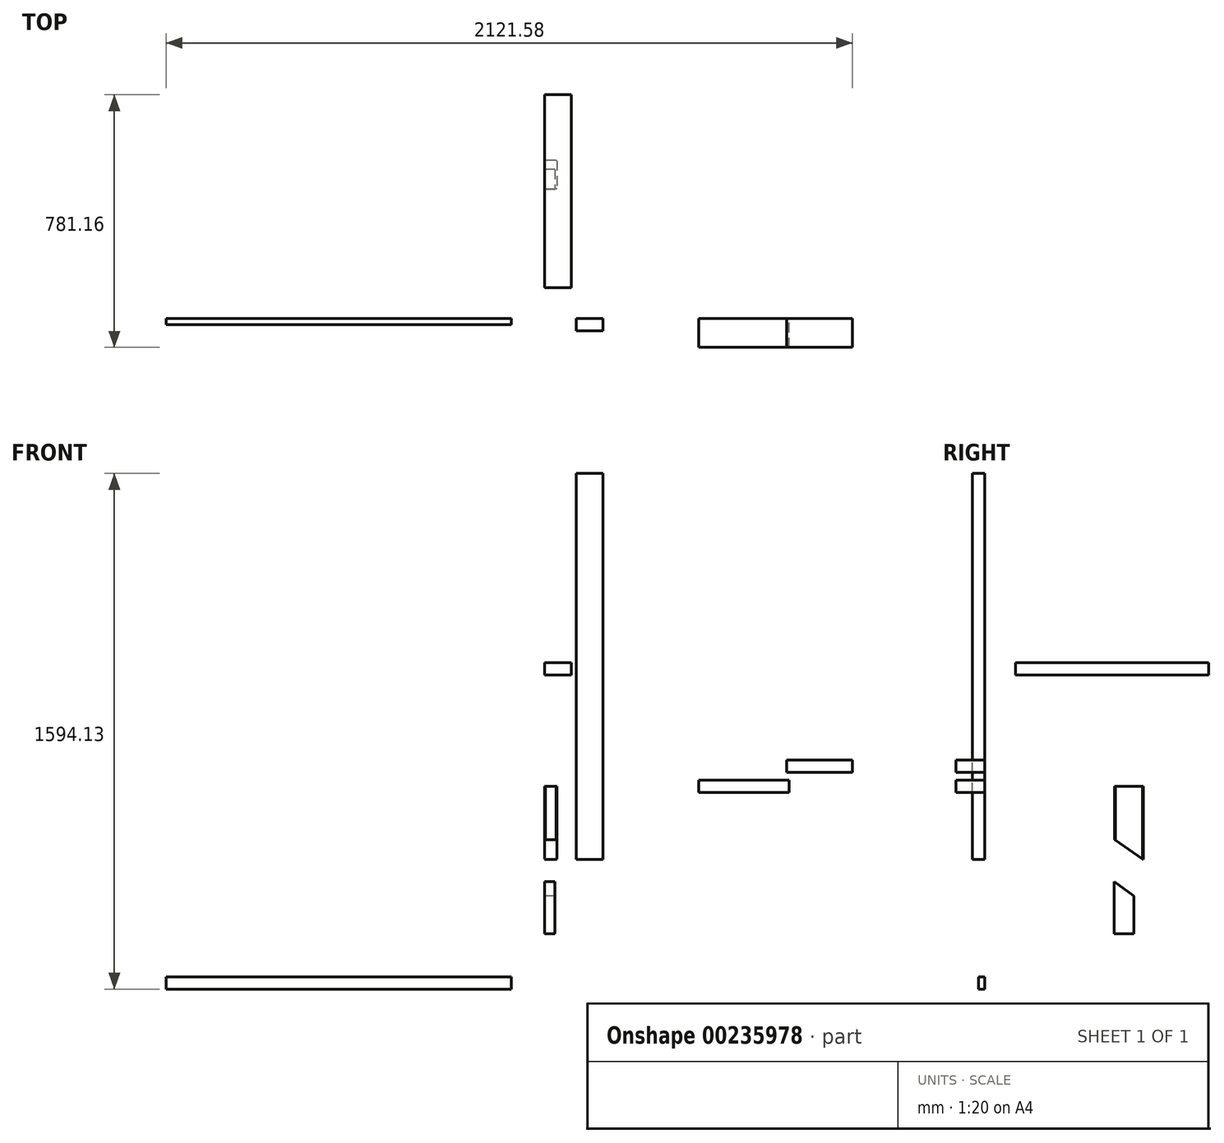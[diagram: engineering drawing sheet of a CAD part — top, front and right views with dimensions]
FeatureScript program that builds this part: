
annotation { "Feature Type Name" : "Feature", "Feature Type Description" : "" }
export const myFeature = defineFeature(function(context is Context, id is Id, definition is map)
    precondition{}
    {
        {
            var Q0;
            Q0=qCreatedBy(makeId("Front.planeOp"),FACE);
            var sketch = newSketch(context, id + "F0", { "sketchPlane" : qUnion([Q0])});
            skLineSegment(sketch, "E0.bottom", {"start": v(0, 0) * mm, "end": v(88.9, 0) * mm});
            skLineSegment(sketch, "E0.top", {"start": v(0, 254) * mm, "end": v(88.9, 254) * mm});
            skLineSegment(sketch, "E0.left", {"start": v(0, 0) * mm, "end": v(0, 254) * mm});
            skLineSegment(sketch, "E0.right", {"start": v(88.9, 0) * mm, "end": v(88.9, 254) * mm});
            skSolve(sketch);
        }
        {
            var Q0;
            Q0 = qSketchRegion(id + "F0", true);
            extrude(context, id + "F1", {"entities" : qUnion([Q0]), "depth" : 38.1 * mm});
        }
        {
            var Q0;
            Q0=makeQuery(id+"F1.opExtrude","CAP_EDGE",EDGE,{"disambiguationData":[OSD([sQuery(id+"F0.wireOp",EDGE,"E0.left")])],"isStart":true});
            var Q1;
            Q1=makeQuery(id+"F1.opExtrude","CAP_EDGE",EDGE,{"disambiguationData":[OSD([sQuery(id+"F0.wireOp",EDGE,"E0.left")])],"isStart":false});
            var Q2;
            Q2=makeQuery(id+"F1.opExtrude","CAP_EDGE",EDGE,{"disambiguationData":[OSD([sQuery(id+"F0.wireOp",EDGE,"E0.right")])],"isStart":false});
            var Q3;
            Q3=makeQuery(id+"F1.opExtrude","CAP_EDGE",EDGE,{"disambiguationData":[OSD([sQuery(id+"F0.wireOp",EDGE,"E0.right")])],"isStart":true});
            fillet(context, id + "F2", {"entities" : qUnion([Q0, Q1, Q2, Q3]), "radius" : 2.54 * mm, "tangentPropagation" : true, "allowEdgeOverflow" : false});
        }
        {
            var Q0;
            Q0=qCreatedBy(makeId("Front.planeOp"),FACE);
            var sketch = newSketch(context, id + "F3", { "sketchPlane" : qUnion([Q0])});
            skLineSegment(sketch, "E1.bottom", {"start": v(98.15, 0) * mm, "end": v(180.7, 0) * mm});
            skLineSegment(sketch, "E1.top", {"start": v(98.15, 1193.8) * mm, "end": v(180.7, 1193.8) * mm});
            skLineSegment(sketch, "E1.left", {"start": v(98.15, 0) * mm, "end": v(98.15, 1193.8) * mm});
            skLineSegment(sketch, "E1.right", {"start": v(180.7, 0) * mm, "end": v(180.7, 1193.8) * mm});
            skSolve(sketch);
        }
        {
            var Q0;
            Q0 = qSketchRegion(id + "F3", true);
            extrude(context, id + "F4", {"entities" : qUnion([Q0]), "depth" : 38.1 * mm});
        }
        {
            var Q0;
            Q0=qCreatedBy(makeId("Right.planeOp"),FACE);
            var sketch = newSketch(context, id + "F5", { "sketchPlane" : qUnion([Q0])});
            skLineSegment(sketch, "E2.top", {"start": v(421.64, 298.64) * mm, "end": v(459.74, 298.64) * mm});
            skLineSegment(sketch, "E2.right", {"start": v(459.74, 44.64) * mm, "end": v(459.74, 298.64) * mm});
            skLineSegment(sketch, "E3", {"start": v(421.64, 298.64) * mm, "end": v(421.64, 82.74) * mm});
            skLineSegment(sketch, "E4", {"start": v(421.64, 82.74) * mm, "end": v(459.74, 44.64) * mm});
            skSolve(sketch);
        }
        {
            var Q0;
            Q0 = qSketchRegion(id + "F5", true);
            extrude(context, id + "F6", {"entities" : qUnion([Q0]), "depth" : 88.9 * mm});
        }
        {
            var Q0;
            Q0=makeQuery(id+"F6.opExtrude","CAP_EDGE",EDGE,{"disambiguationData":[OSD([sQuery(id+"F5.wireOp",EDGE,"E3")])],"isStart":false});
            var Q1;
            Q1=makeQuery(id+"F6.opExtrude","CAP_EDGE",EDGE,{"disambiguationData":[OSD([sQuery(id+"F5.wireOp",EDGE,"E2.right")])],"isStart":false});
            var Q2;
            Q2=makeQuery(id+"F6.opExtrude","CAP_EDGE",EDGE,{"disambiguationData":[OSD([sQuery(id+"F5.wireOp",EDGE,"E3")])],"isStart":true});
            var Q3;
            Q3=makeQuery(id+"F6.opExtrude","CAP_EDGE",EDGE,{"disambiguationData":[OSD([sQuery(id+"F5.wireOp",EDGE,"E2.right")])],"isStart":true});
            fillet(context, id + "F7", {"entities" : qUnion([Q0, Q1, Q2, Q3]), "radius" : 2.54 * mm, "tangentPropagation" : true, "allowEdgeOverflow" : false});
        }
        {
            var Q0;
            Q0=qCreatedBy(makeId("Right.planeOp"),FACE);
            var sketch = newSketch(context, id + "F8", { "sketchPlane" : qUnion([Q0])});
            skLineSegment(sketch, "E5.top", {"start": v(427.99, -255.27) * mm, "end": v(466.09, -255.27) * mm});
            skLineSegment(sketch, "E5.left", {"start": v(427.99, -1.27) * mm, "end": v(427.99, -255.27) * mm});
            skLineSegment(sketch, "E6", {"start": v(466.09, -255.27) * mm, "end": v(466.09, -39.37) * mm});
            skLineSegment(sketch, "E7", {"start": v(466.09, -39.37) * mm, "end": v(427.99, -1.27) * mm});
            skSolve(sketch);
        }
        {
            var Q0;
            Q0 = qSketchRegion(id + "F8", true);
            extrude(context, id + "F9", {"entities" : qUnion([Q0]), "depth" : 88.9 * mm});
        }
        {
            var Q0;
            Q0=makeQuery(id+"F9.opExtrude","CAP_EDGE",EDGE,{"disambiguationData":[OSD([sQuery(id+"F8.wireOp",EDGE,"E5.left")])],"isStart":true});
            var Q1;
            Q1=makeQuery(id+"F9.opExtrude","CAP_EDGE",EDGE,{"disambiguationData":[OSD([sQuery(id+"F8.wireOp",EDGE,"E5.left")])],"isStart":false});
            var Q2;
            Q2=makeQuery(id+"F9.opExtrude","CAP_EDGE",EDGE,{"disambiguationData":[OSD([sQuery(id+"F8.wireOp",EDGE,"E6")])],"isStart":false});
            var Q3;
            Q3=makeQuery(id+"F9.opExtrude","CAP_EDGE",EDGE,{"disambiguationData":[OSD([sQuery(id+"F8.wireOp",EDGE,"E6")])],"isStart":true});
            fillet(context, id + "F10", {"entities" : qUnion([Q0, Q1, Q2, Q3]), "radius" : 2.54 * mm, "tangentPropagation" : true, "allowEdgeOverflow" : false});
        }
        {
            var Q0;
            Q0=makeQuery(id+"F1.opExtrude","SWEPT_BODY",BODY,{"disambiguationData":[OSD([sQuery(id+"F0.wireOp",EDGE,"E0.bottom"),sQuery(id+"F0.wireOp",EDGE,"E0.top"),sQuery(id+"F0.wireOp",EDGE,"E0.left"),sQuery(id+"F0.wireOp",EDGE,"E0.right")])]});
            deleteBodies(context, id + "F11", {"entities" : qUnion([Q0])});
        }
        {
            var Q0;
            Q0=makeQuery(id+"F6.opExtrude","SWEPT_BODY",BODY,{"disambiguationData":[OSD([sQuery(id+"F5.wireOp",EDGE,"E2.top"),sQuery(id+"F5.wireOp",EDGE,"E2.right"),sQuery(id+"F5.wireOp",EDGE,"E3"),sQuery(id+"F5.wireOp",EDGE,"E4")])]});
            deleteBodies(context, id + "F12", {"entities" : qUnion([Q0])});
        }
        {
            var Q0;
            Q0=makeQuery(id+"F9.opExtrude","SWEPT_BODY",BODY,{"disambiguationData":[OSD([sQuery(id+"F8.wireOp",EDGE,"E5.top"),sQuery(id+"F8.wireOp",EDGE,"E5.left"),sQuery(id+"F8.wireOp",EDGE,"E6"),sQuery(id+"F8.wireOp",EDGE,"E7")])]});
            deleteBodies(context, id + "F13", {"entities" : qUnion([Q0])});
        }
        {
            var Q0;
            Q0=qCreatedBy(makeId("Right.planeOp"),FACE);
            var sketch = newSketch(context, id + "F14", { "sketchPlane" : qUnion([Q0])});
            skLineSegment(sketch, "E8.top", {"start": v(489.61, 227.18) * mm, "end": v(400.71, 227.18) * mm});
            skLineSegment(sketch, "E8.left", {"start": v(489.61, 0) * mm, "end": v(489.61, 227.18) * mm});
            skLineSegment(sketch, "E9", {"start": v(400.71, 227.18) * mm, "end": v(400.71, 62.08) * mm});
            skLineSegment(sketch, "E10", {"start": v(400.71, 62.08) * mm, "end": v(489.61, 0) * mm});
            skSolve(sketch);
        }
        {
            var Q0;
            Q0 = qSketchRegion(id + "F14", true);
            extrude(context, id + "F15", {"entities" : qUnion([Q0]), "depth" : 38.1 * mm});
        }
        {
            var Q0;
            Q0=makeQuery(id+"F15.opExtrude","CAP_EDGE",EDGE,{"disambiguationData":[OSD([sQuery(id+"F14.wireOp",EDGE,"E9")])],"isStart":false});
            var Q1;
            Q1=makeQuery(id+"F15.opExtrude","CAP_EDGE",EDGE,{"disambiguationData":[OSD([sQuery(id+"F14.wireOp",EDGE,"E8.left")])],"isStart":false});
            var Q2;
            Q2=makeQuery(id+"F15.opExtrude","CAP_EDGE",EDGE,{"disambiguationData":[OSD([sQuery(id+"F14.wireOp",EDGE,"E8.left")])],"isStart":true});
            var Q3;
            Q3=makeQuery(id+"F15.opExtrude","CAP_EDGE",EDGE,{"disambiguationData":[OSD([sQuery(id+"F14.wireOp",EDGE,"E9")])],"isStart":true});
            chamfer(context, id + "F16", {"entities" : qUnion([Q0, Q1, Q2, Q3]), "width" : 2.54 * mm, "tangentPropagation" : true});
        }
        {
            var Q0;
            Q0=qCreatedBy(makeId("Right.planeOp"),FACE);
            var sketch = newSketch(context, id + "F17", { "sketchPlane" : qUnion([Q0])});
            skLineSegment(sketch, "E11.top", {"start": v(374.35, 547.37) * mm, "end": v(463.25, 547.37) * mm});
            skLineSegment(sketch, "E11.right", {"start": v(463.25, 775.97) * mm, "end": v(463.25, 547.37) * mm});
            skLineSegment(sketch, "E12", {"start": v(374.35, 547.37) * mm, "end": v(374.35, 712.47) * mm});
            skLineSegment(sketch, "E13", {"start": v(374.35, 712.47) * mm, "end": v(463.25, 775.97) * mm});
            skSolve(sketch);
        }
        {
            var Q0;
            Q0 = qSketchRegion(id + "F17", true);
            extrude(context, id + "F18", {"entities" : qUnion([Q0]), "depth" : 38.1 * mm});
        }
        {
            var Q0;
            Q0=makeQuery(id+"F18.opExtrude","CAP_EDGE",EDGE,{"disambiguationData":[OSD([sQuery(id+"F17.wireOp",EDGE,"E12")])],"isStart":true});
            var Q1;
            Q1=makeQuery(id+"F18.opExtrude","CAP_EDGE",EDGE,{"disambiguationData":[OSD([sQuery(id+"F17.wireOp",EDGE,"E12")])],"isStart":false});
            var Q2;
            Q2=makeQuery(id+"F18.opExtrude","CAP_EDGE",EDGE,{"disambiguationData":[OSD([sQuery(id+"F17.wireOp",EDGE,"E11.right")])],"isStart":false});
            var Q3;
            Q3=makeQuery(id+"F18.opExtrude","CAP_EDGE",EDGE,{"disambiguationData":[OSD([sQuery(id+"F17.wireOp",EDGE,"E11.right")])],"isStart":true});
            chamfer(context, id + "F19", {"entities" : qUnion([Q0, Q1, Q2, Q3]), "width" : 2.54 * mm, "tangentPropagation" : true});
        }
        {
            var Q0;
            Q0=makeQuery(id+"F18.opExtrude","SWEPT_BODY",BODY,{"disambiguationData":[OSD([sQuery(id+"F17.wireOp",EDGE,"E11.top"),sQuery(id+"F17.wireOp",EDGE,"E11.right"),sQuery(id+"F17.wireOp",EDGE,"E12"),sQuery(id+"F17.wireOp",EDGE,"E13")])]});
            deleteBodies(context, id + "F20", {"entities" : qUnion([Q0])});
        }
        {
            var Q0;
            Q0=qCreatedBy(makeId("Right.planeOp"),FACE);
            var sketch = newSketch(context, id + "F21", { "sketchPlane" : qUnion([Q0])});
            skLineSegment(sketch, "E14.left", {"start": v(399.53, -68.15) * mm, "end": v(399.53, -229.61) * mm});
            skLineSegment(sketch, "E15", {"start": v(460.88, -111.97) * mm, "end": v(399.53, -68.15) * mm});
            skLineSegment(sketch, "E16", {"start": v(460.88, -229.61) * mm, "end": v(460.88, -111.97) * mm});
            skLineSegment(sketch, "E17", {"start": v(460.88, -229.61) * mm, "end": v(399.53, -229.61) * mm});
            skPoint(sketch, "E18.orphan", {"position": v(399.53, -271.35) * mm});
            skSolve(sketch);
        }
        {
            var Q0;
            Q0 = qSketchRegion(id + "F21", true);
            extrude(context, id + "F22", {"entities" : qUnion([Q0]), "depth" : 31.75 * mm});
        }
        {
            var Q0;
            Q0=qCreatedBy(makeId("Right.planeOp"),FACE);
            var sketch = newSketch(context, id + "F23", { "sketchPlane" : qUnion([Q0])});
            skLineSegment(sketch, "E19.bottom", {"start": v(95.36, 571.11) * mm, "end": v(692.26, 571.11) * mm});
            skLineSegment(sketch, "E19.top", {"start": v(95.36, 609.21) * mm, "end": v(692.26, 609.21) * mm});
            skLineSegment(sketch, "E19.left", {"start": v(95.36, 571.11) * mm, "end": v(95.36, 609.21) * mm});
            skLineSegment(sketch, "E19.right", {"start": v(692.26, 571.11) * mm, "end": v(692.26, 609.21) * mm});
            skSolve(sketch);
        }
        {
            var Q0;
            Q0 = qSketchRegion(id + "F23", true);
            extrude(context, id + "F24", {"entities" : qUnion([Q0]), "depth" : 82.55 * mm});
        }
        {
            var Q0;
            Q0=qCreatedBy(makeId("Front.planeOp"),FACE);
            var sketch = newSketch(context, id + "F25", { "sketchPlane" : qUnion([Q0])});
            skLineSegment(sketch, "E20.bottom", {"start": v(476.01, 245.48) * mm, "end": v(755.41, 245.48) * mm});
            skLineSegment(sketch, "E20.top", {"start": v(476.01, 207.38) * mm, "end": v(755.41, 207.38) * mm});
            skLineSegment(sketch, "E20.left", {"start": v(476.01, 245.48) * mm, "end": v(476.01, 207.38) * mm});
            skLineSegment(sketch, "E20.right", {"start": v(755.41, 245.48) * mm, "end": v(755.41, 207.38) * mm});
            skSolve(sketch);
        }
        {
            var Q0;
            Q0 = qSketchRegion(id + "F25", true);
            extrude(context, id + "F26", {"entities" : qUnion([Q0]), "depth" : 88.9 * mm});
        }
        {
            var Q0;
            Q0=qCreatedBy(makeId("Front.planeOp"),FACE);
            var sketch = newSketch(context, id + "F27", { "sketchPlane" : qUnion([Q0])});
            skLineSegment(sketch, "E21.bottom", {"start": v(748.64, 308.1) * mm, "end": v(951.84, 308.1) * mm});
            skLineSegment(sketch, "E21.top", {"start": v(748.64, 270) * mm, "end": v(951.84, 270) * mm});
            skLineSegment(sketch, "E21.left", {"start": v(748.64, 308.1) * mm, "end": v(748.64, 270) * mm});
            skLineSegment(sketch, "E21.right", {"start": v(951.84, 308.1) * mm, "end": v(951.84, 270) * mm});
            skSolve(sketch);
        }
        {
            var Q0;
            Q0 = qSketchRegion(id + "F27", true);
            extrude(context, id + "F28", {"entities" : qUnion([Q0]), "depth" : 88.9 * mm});
        }
        {
            var Q0;
            Q0=qCreatedBy(makeId("Front.planeOp"),FACE);
            var sketch = newSketch(context, id + "F29", { "sketchPlane" : qUnion([Q0])});
            skLineSegment(sketch, "E22.bottom", {"start": v(-1169.74, -362.23) * mm, "end": v(-102.94, -362.23) * mm});
            skLineSegment(sketch, "E22.top", {"start": v(-1169.74, -400.33) * mm, "end": v(-102.94, -400.33) * mm});
            skLineSegment(sketch, "E22.left", {"start": v(-1169.74, -362.23) * mm, "end": v(-1169.74, -400.33) * mm});
            skLineSegment(sketch, "E22.right", {"start": v(-102.94, -362.23) * mm, "end": v(-102.94, -400.33) * mm});
            skSolve(sketch);
        }
        {
            var Q0;
            Q0 = qSketchRegion(id + "F29", true);
            extrude(context, id + "F30", {"entities" : qUnion([Q0]), "depth" : 19.05 * mm});
        }
    });
